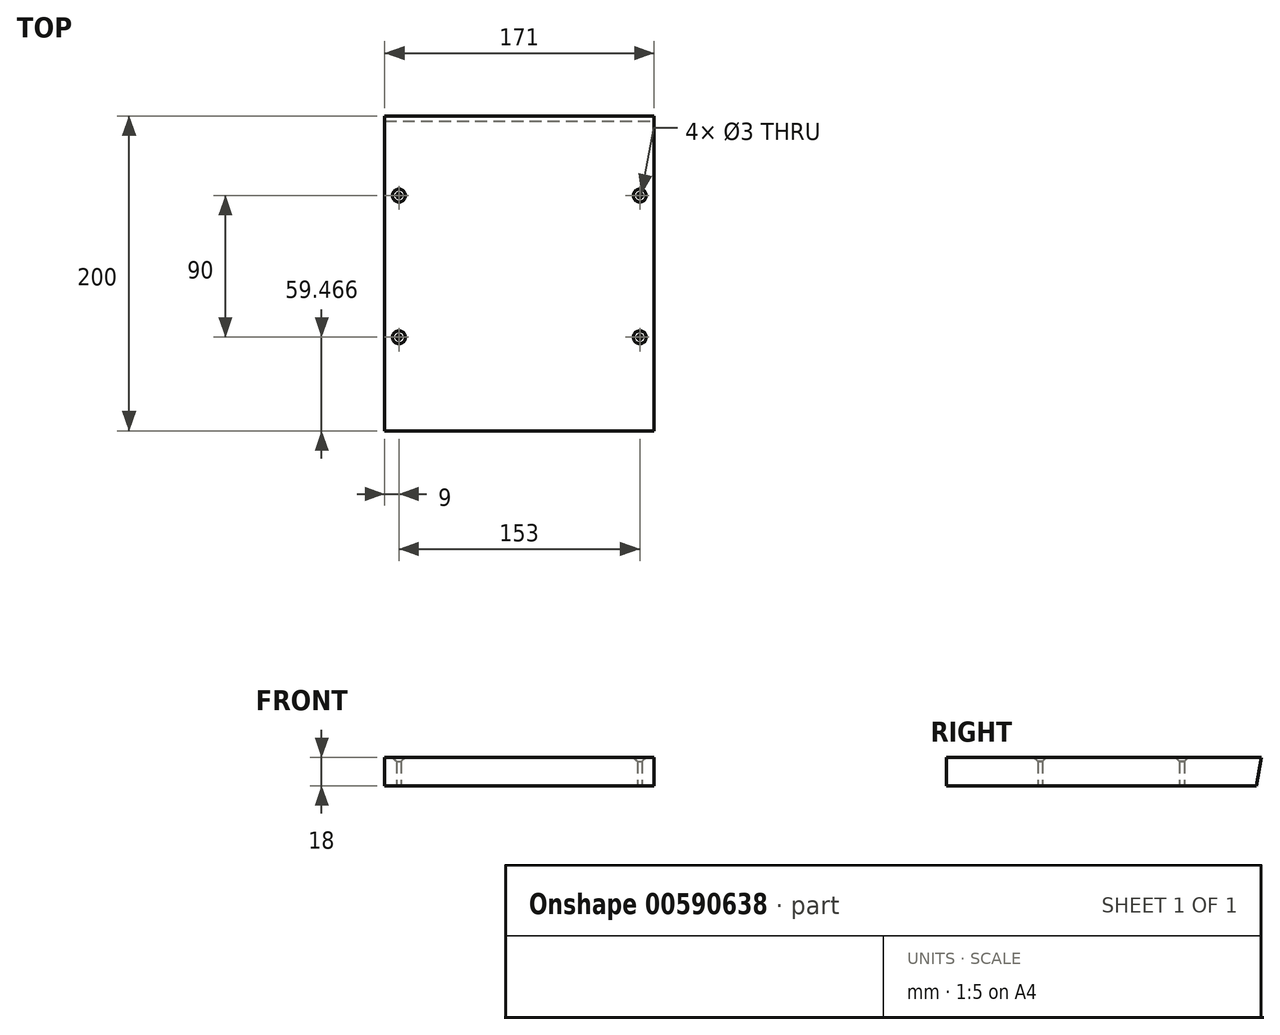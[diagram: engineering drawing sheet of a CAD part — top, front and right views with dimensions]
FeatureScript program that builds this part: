
annotation { "Feature Type Name" : "Feature", "Feature Type Description" : "" }
export const myFeature = defineFeature(function(context is Context, id is Id, definition is map)
    precondition{}
    {
        {
            var Q0;
            Q0=qCreatedBy(makeId("Top.planeOp"),FACE);
            var sketch = newSketch(context, id + "F0", { "sketchPlane" : qUnion([Q0])});
            skLineSegment(sketch, "E0.bottom", {"start": v(85.5, -100) * mm, "end": v(-85.5, -100) * mm});
            skLineSegment(sketch, "E0.top", {"start": v(85.5, 100) * mm, "end": v(-85.5, 100) * mm});
            skLineSegment(sketch, "E0.left", {"start": v(85.5, -100) * mm, "end": v(85.5, 100) * mm});
            skLineSegment(sketch, "E0.right", {"start": v(-85.5, -100) * mm, "end": v(-85.5, 100) * mm});
            skPoint(sketch, "E0.middle", {"position": v(0, 0) * mm});
            skSolve(sketch);
        }
        {
            var Q0;
            Q0=makeQuery(id+"F0.imprint","IMPRINT",FACE,{"disambiguationData":[TD([[makeQuery(id+"F0.imprint","IMPRINT",EDGE,{"derivedFrom":sQuery(id+"F0.wireOp",EDGE,"E0.bottom")}),-1.0]])]});
            extrude(context, id + "F1", {"entities" : qUnion([Q0]), "depth" : 18 * mm, "offsetDistance" : 25 * mm});
        }
        {
            var Q0;
            Q0=makeQuery(id+"F1.opExtrude","SWEPT_FACE",FACE,{"disambiguationData":[OSD([sQuery(id+"F0.wireOp",EDGE,"E0.left")])]});
            var sketch = newSketch(context, id + "F2", { "sketchPlane" : qUnion([Q0])});
            skLineSegment(sketch, "E1", {"start": v(100, 18) * mm, "end": v(96.83, 0) * mm});
            skLineSegment(sketch, "E2", {"start": v(100, 18) * mm, "end": v(100, 0) * mm});
            skLineSegment(sketch, "E3", {"start": v(100, 0) * mm, "end": v(96.83, 0) * mm});
            skSolve(sketch);
        }
        {
            var Q0;
            Q0=makeQuery(id+"F2.imprint","IMPRINT",FACE,{"disambiguationData":[TD([[makeQuery(id+"F2.imprint","IMPRINT",EDGE,{"derivedFrom":sQuery(id+"F2.wireOp",EDGE,"E1")}),1.0]])]});
            extrude(context, id + "F3", {"entities" : qUnion([Q0]), "operationType" : NewBodyOperationType.REMOVE, "endBound" : BoundingType.THROUGH_ALL, "oppositeDirection" : true, "depth" : 25 * mm, "offsetDistance" : 25 * mm});
        }
        {
            var Q0;
            Q0=makeQuery(id+"F1.opExtrude","CAP_FACE",FACE,{"disambiguationData":[OSD([sQuery(id+"F0.wireOp",EDGE,"E0.bottom"),sQuery(id+"F0.wireOp",EDGE,"E0.top"),sQuery(id+"F0.wireOp",EDGE,"E0.left"),sQuery(id+"F0.wireOp",EDGE,"E0.right")])],"isStart":false});
            var sketch = newSketch(context, id + "F4", { "sketchPlane" : qUnion([Q0])});
            skPoint(sketch, "E4", {"position": v(-76.5, 49.47) * mm});
            skPoint(sketch, "E5", {"position": v(76.5, 49.47) * mm});
            skPoint(sketch, "E6", {"position": v(76.5, -40.53) * mm});
            skPoint(sketch, "E7", {"position": v(-76.5, -40.53) * mm});
            skSolve(sketch);
        }
        {
            var Q0;
            Q0=sQuery(id+"F4.wireOp",VERTEX,"E4");
            var Q1;
            Q1=sQuery(id+"F4.wireOp",VERTEX,"E5");
            var Q2;
            Q2=makeQuery(id+"F1.opExtrude","SWEPT_BODY",BODY,{"disambiguationData":[OSD([sQuery(id+"F0.wireOp",EDGE,"E0.bottom"),sQuery(id+"F0.wireOp",EDGE,"E0.top"),sQuery(id+"F0.wireOp",EDGE,"E0.left"),sQuery(id+"F0.wireOp",EDGE,"E0.right")])]});
            hole(context, id + "F5", {"style" : HoleStyle.C_SINK, "endStyle" : HoleEndStyle.THROUGH, "holeDiameter" : 3 * mm, "cSinkDiameter" : 8.2 * mm, "cSinkAngle" : 90 * degree, "majorDiameter" : 5 * mm, "isTappedThrough" : true, "tappedDepth" : 12 * mm, "tapClearance" : 3, "locations" : qUnion([Q0, Q1]), "scope" : qUnion([Q2])});
        }
        {
            var Q0;
            Q0=sQuery(id+"F4.wireOp",VERTEX,"E7");
            var Q1;
            Q1=sQuery(id+"F4.wireOp",VERTEX,"E6");
            var Q2;
            Q2=makeQuery(id+"F1.opExtrude","SWEPT_BODY",BODY,{"disambiguationData":[OSD([sQuery(id+"F0.wireOp",EDGE,"E0.bottom"),sQuery(id+"F0.wireOp",EDGE,"E0.top"),sQuery(id+"F0.wireOp",EDGE,"E0.left"),sQuery(id+"F0.wireOp",EDGE,"E0.right")])]});
            hole(context, id + "F6", {"style" : HoleStyle.C_SINK, "endStyle" : HoleEndStyle.THROUGH, "holeDiameter" : 3 * mm, "cSinkDiameter" : 8.2 * mm, "cSinkAngle" : 90 * degree, "majorDiameter" : 5 * mm, "isTappedThrough" : true, "tappedDepth" : 12 * mm, "tapClearance" : 3, "locations" : qUnion([Q0, Q1]), "scope" : qUnion([Q2])});
        }
    });
